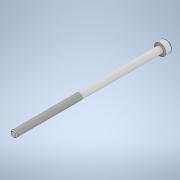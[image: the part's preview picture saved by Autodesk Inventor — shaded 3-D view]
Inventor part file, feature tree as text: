
AUTODESK INVENTOR PART (.ipt)
format: ipt  version: 2020 (Build 240168000, 168)  size: 122,880 bytes
history: native  units: mm
features: sketch x2, revolve x1, chamfer x1, thread x1, extrude x1
ambient origin geometry x8: Origin, YZ Plane, XZ Plane, XY Plane, X Axis, Y Axis, Z Axis, Center Point
bodies: Solid1 (feature_tree)
feature tree (6):
  revolve  "Revolution1"  [1 undecoded]
  chamfer  "Chamfer1"  Distance=4.0mm
  thread  "Thread1"  [1 undecoded]
  extrude  "Extrusion1"  Depth=2.0mm TaperAngle=45.0deg
  sketch  "Sketch1"  dims[d0=2.0mm d1=90.0mm]
  sketch  "Sketch2"  dims[d2=3.5mm d3=4.0mm d4=90.0deg d5=0.5mm d6=2.0mm d7=45.0deg d8=40.0mm d9=0.0mm d10=1.5mm d11=60.0mm d13=360.0deg d15=2.0mm d16=0.0mm]
note: 2 required parameter values undecoded (feature->parameter linkage not recoverable at this tier; creation-order binding heuristic only, values carry confidence <= 0.55)